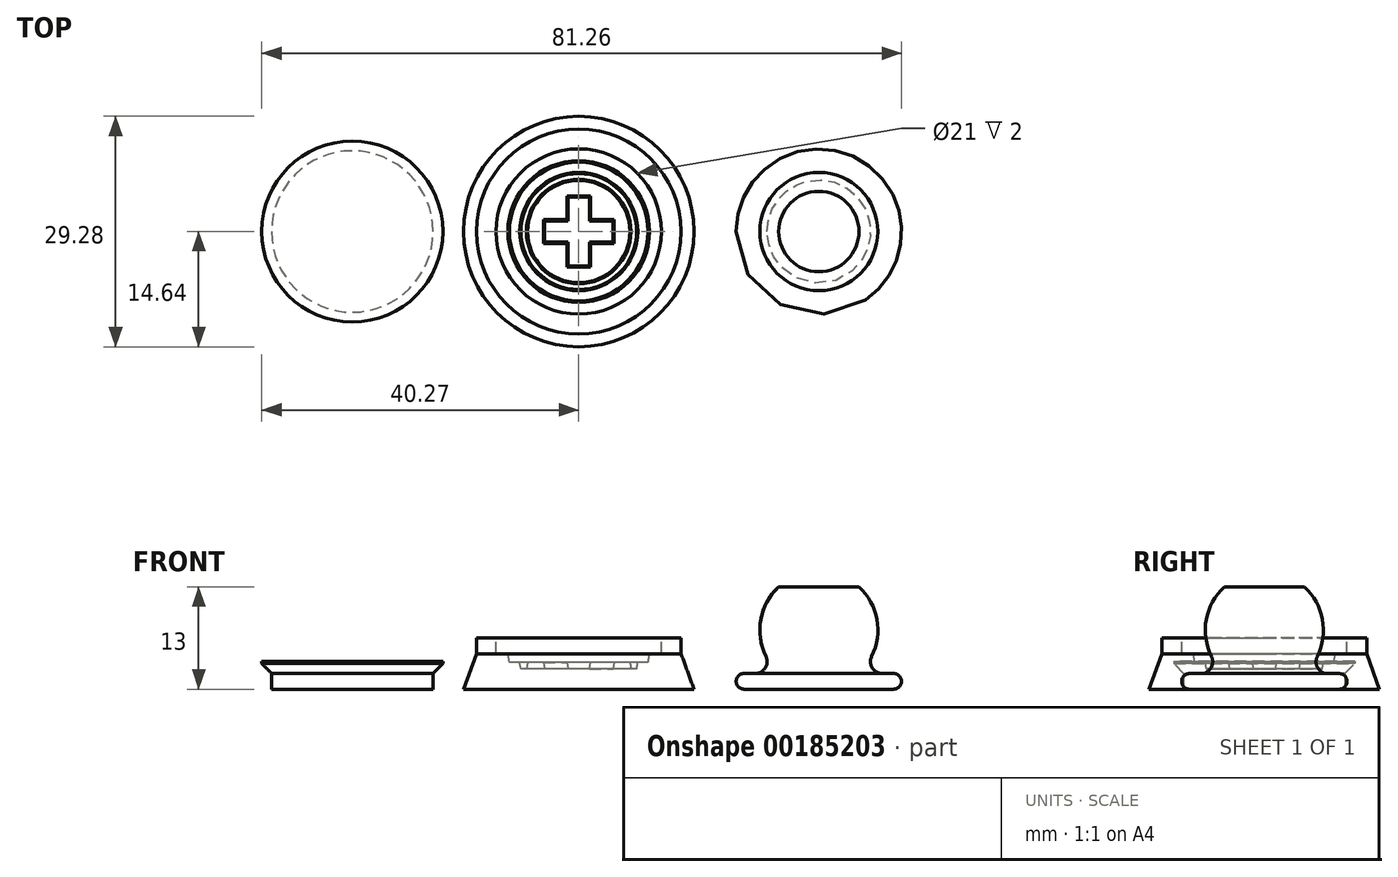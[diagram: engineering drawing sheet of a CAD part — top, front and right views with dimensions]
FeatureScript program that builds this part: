
annotation { "Feature Type Name" : "Feature", "Feature Type Description" : "" }
export const myFeature = defineFeature(function(context is Context, id is Id, definition is map)
    precondition{}
    {
        {
            var Q0;
            Q0=qCreatedBy(makeId("Front.planeOp"),FACE);
            var sketch = newSketch(context, id + "F0", { "sketchPlane" : qUnion([Q0])});
            skLineSegment(sketch, "E0.bottom", {"start": v(-13, 1) * mm, "end": v(0, 1) * mm});
            skLineSegment(sketch, "E0.top", {"start": v(-14.64, -3.5) * mm, "end": v(0, -3.5) * mm});
            skLineSegment(sketch, "E0.right", {"start": v(0, 1) * mm, "end": v(0, -3.5) * mm});
            skLineSegment(sketch, "E1", {"start": v(0, 7.32) * mm, "end": v(0, -8.04) * mm, "construction": true});
            skLineSegment(sketch, "E2", {"start": v(-13, 1) * mm, "end": v(-14.64, -3.5) * mm});
            skSolve(sketch);
        }
        {
            var Q0;
            Q0=makeQuery(id+"F0.imprint","IMPRINT",FACE,{"disambiguationData":[TD([[makeQuery(id+"F0.imprint","IMPRINT",EDGE,{"derivedFrom":sQuery(id+"F0.wireOp",EDGE,"E0.bottom")}),-1.0]])]});
            var Q1;
            Q1=sQuery(id+"F0.wireOp",EDGE,"E1");
            revolve(context, id + "F1", {"entities" : qUnion([Q0]), "axis" : qUnion([Q1]), "revolveType" : RevolveType.FULL});
        }
        {
            var Q0;
            Q0=makeQuery(id+"F1.opRevolve","SWEPT_FACE",FACE,{"disambiguationData":[OSD([sQuery(id+"F0.wireOp",EDGE,"E0.bottom")])]});
            var sketch = newSketch(context, id + "F2", { "sketchPlane" : qUnion([Q0])});
            skCircle(sketch, "E3", {"center": v(0, 0) * mm, "radius": 9 * mm});
            skSolve(sketch);
        }
        {
            var Q0;
            Q0=makeQuery(id+"F2.imprint","IMPRINT",FACE,{"disambiguationData":[TD([[makeQuery(id+"F2.imprint","IMPRINT",EDGE,{"derivedFrom":sQuery(id+"F2.wireOp",EDGE,"E3")}),1.0]])]});
            extrude(context, id + "F3", {"entities" : qUnion([Q0]), "operationType" : NewBodyOperationType.REMOVE, "oppositeDirection" : true, "depth" : 1.1 * mm, "hasDraft" : true, "draftAngle" : 10 * degree, "draftPullDirection" : true});
        }
        {
            var Q0;
            Q0=makeQuery(id+"F3.boolean.opBoolean","COPY",FACE,{"derivedFrom":makeQuery(id+"F3.opExtrude","CAP_FACE",FACE,{"disambiguationData":[OSD([sQuery(id+"F2.wireOp",EDGE,"E3")])],"isStart":false})});
            var sketch = newSketch(context, id + "F4", { "sketchPlane" : qUnion([Q0])});
            skCircle(sketch, "E4", {"center": v(0, 0) * mm, "radius": 7.5 * mm});
            skCircle(sketch, "E5", {"center": v(0, 0) * mm, "radius": 6.5 * mm});
            skLineSegment(sketch, "E6.bottom", {"start": v(-1.5, 4.5) * mm, "end": v(1.5, 4.5) * mm});
            skLineSegment(sketch, "E6.top", {"start": v(-1.5, -4.5) * mm, "end": v(1.5, -4.5) * mm});
            skLineSegment(sketch, "E6.left", {"start": v(-1.5, 4.5) * mm, "end": v(-1.5, 1.5) * mm});
            skLineSegment(sketch, "E6.right", {"start": v(1.5, 4.5) * mm, "end": v(1.5, 1.5) * mm});
            skLineSegment(sketch, "E7.bottom", {"start": v(-4.5, 1.5) * mm, "end": v(-1.5, 1.5) * mm});
            skLineSegment(sketch, "E7.top", {"start": v(-4.5, -1.5) * mm, "end": v(-1.5, -1.5) * mm});
            skLineSegment(sketch, "E7.left", {"start": v(-4.5, 1.5) * mm, "end": v(-4.5, -1.5) * mm});
            skLineSegment(sketch, "E7.right", {"start": v(4.5, 1.5) * mm, "end": v(4.5, -1.5) * mm});
            skLineSegment(sketch, "E8.trimOffspring", {"start": v(1.5, 1.5) * mm, "end": v(4.5, 1.5) * mm});
            skLineSegment(sketch, "E9.trimOffspring", {"start": v(-1.5, -1.5) * mm, "end": v(-1.5, -4.5) * mm});
            skLineSegment(sketch, "E10.trimOffspring", {"start": v(1.5, -1.5) * mm, "end": v(4.5, -1.5) * mm});
            skLineSegment(sketch, "E11.trimOffspring", {"start": v(1.5, -1.5) * mm, "end": v(1.5, -4.5) * mm});
            skSolve(sketch);
        }
        {
            var Q0;
            Q0=makeQuery(id+"F4.imprint","IMPRINT",FACE,{"disambiguationData":[TD([[makeQuery(id+"F4.imprint","IMPRINT",EDGE,{"derivedFrom":sQuery(id+"F4.wireOp",EDGE,"E6.bottom")}),-1.0]])]});
            var Q1;
            Q1=makeQuery(id+"F4.imprint","IMPRINT",FACE,{"disambiguationData":[TD([[makeQuery(id+"F4.imprint","IMPRINT",EDGE,{"derivedFrom":sQuery(id+"F4.wireOp",EDGE,"E4")}),1.0]])]});
            extrude(context, id + "F5", {"entities" : qUnion([Q0, Q1]), "operationType" : NewBodyOperationType.REMOVE, "oppositeDirection" : true, "depth" : .8 * mm, "hasDraft" : true, "draftAngle" : 10 * degree, "draftPullDirection" : true});
        }
        {
            var Q0;
            Q0=qCreatedBy(makeId("Front.planeOp"),FACE);
            var sketch = newSketch(context, id + "F6", { "sketchPlane" : qUnion([Q0])});
            skLineSegment(sketch, "E12", {"start": v(0, 6.95) * mm, "end": v(0, -3.6) * mm, "construction": true});
            skLineSegment(sketch, "E13.bottom", {"start": v(-13, 3) * mm, "end": v(-10.5, 3) * mm});
            skLineSegment(sketch, "E13.top", {"start": v(-13, 1) * mm, "end": v(-10.5, 1) * mm});
            skLineSegment(sketch, "E13.left", {"start": v(-13, 3) * mm, "end": v(-13, 1) * mm});
            skLineSegment(sketch, "E13.right", {"start": v(-10.5, 3) * mm, "end": v(-10.5, 1) * mm});
            skSolve(sketch);
        }
        {
            var Q0;
            Q0=makeQuery(id+"F6.imprint","IMPRINT",FACE,{"disambiguationData":[TD([[makeQuery(id+"F6.imprint","IMPRINT",EDGE,{"derivedFrom":sQuery(id+"F6.wireOp",EDGE,"E13.bottom")}),-1.0]])]});
            var Q1;
            Q1=sQuery(id+"F6.wireOp",EDGE,"E12");
            revolve(context, id + "F7", {"operationType" : NewBodyOperationType.ADD, "entities" : qUnion([Q0]), "axis" : qUnion([Q1]), "revolveType" : RevolveType.FULL});
        }
        {
            var Q0;
            Q0=qCreatedBy(makeId("Front.planeOp"),FACE);
            var sketch = newSketch(context, id + "F8", { "sketchPlane" : qUnion([Q0])});
            skLineSegment(sketch, "E14.top", {"start": v(-39.02, -3.5) * mm, "end": v(-28.77, -3.5) * mm});
            skLineSegment(sketch, "E14.left", {"start": v(-39.02, -1.5) * mm, "end": v(-39.02, -3.5) * mm});
            skLineSegment(sketch, "E14.right", {"start": v(-28.77, -1.3) * mm, "end": v(-28.77, -3.5) * mm});
            skLineSegment(sketch, "E15", {"start": v(-28.77, -6.34) * mm, "end": v(-28.77, 2.62) * mm, "construction": true});
            skLineSegment(sketch, "E16.bottom", {"start": v(-28.77, 0) * mm, "end": v(-40.27, 0) * mm});
            skLineSegment(sketch, "E16.left", {"start": v(-28.77, 0) * mm, "end": v(-28.77, -1.3) * mm});
            skLineSegment(sketch, "E16.right", {"start": v(-40.27, 0) * mm, "end": v(-40.27, -0.25) * mm});
            skLineSegment(sketch, "E17", {"start": v(-40.27, -0.25) * mm, "end": v(-39.02, -1.5) * mm});
            skSolve(sketch);
        }
        {
            var Q0;
            Q0=makeQuery(id+"F8.imprint","IMPRINT",FACE,{"disambiguationData":[TD([[makeQuery(id+"F8.imprint","IMPRINT",EDGE,{"derivedFrom":sQuery(id+"F8.wireOp",EDGE,"E14.top")}),1.0]])]});
            var Q1;
            Q1=sQuery(id+"F8.wireOp",EDGE,"E15");
            revolve(context, id + "F9", {"entities" : qUnion([Q0]), "axis" : qUnion([Q1]), "revolveType" : RevolveType.FULL});
        }
        {
            var Q0;
            Q0=qCreatedBy(makeId("Front.planeOp"),FACE);
            var sketch = newSketch(context, id + "F10", { "sketchPlane" : qUnion([Q0])});
            skLineSegment(sketch, "E18.bottom", {"start": v(21, -1.5) * mm, "end": v(22.43, -1.5) * mm});
            skLineSegment(sketch, "E18.top", {"start": v(21, -3.5) * mm, "end": v(30.5, -3.5) * mm});
            skLineSegment(sketch, "E18.left", {"start": v(20, -2.5) * mm, "end": v(20, -2.5) * mm});
            skLineSegment(sketch, "E19", {"start": v(30.5, -7.79) * mm, "end": v(30.5, -5.66) * mm, "construction": true});
            skArc(sketch, "E20", {"start": v(25.4, 9.5) * mm, "mid": v(23.12, 5.35) * mm, "end": v(23.78, 0.67) * mm});
            skLineSegment(sketch, "E21", {"start": v(30.5, 9.5) * mm, "end": v(30.5, -3.5) * mm});
            skPoint(sketch, "E22.visualSharp", {"position": v(25.4, -1.5) * mm});
            skArc(sketch, "E22.filletArc", {"start": v(22.43, -1.5) * mm, "mid": v(23.7, -0.8) * mm, "end": v(23.78, 0.67) * mm});
            skPoint(sketch, "E23.visualSharp", {"position": v(20, -1.5) * mm});
            skArc(sketch, "E23.filletArc", {"start": v(21, -1.5) * mm, "mid": v(20.29, -1.8) * mm, "end": v(20, -2.5) * mm});
            skPoint(sketch, "E24.visualSharp", {"position": v(20, -3.5) * mm});
            skArc(sketch, "E24.filletArc", {"start": v(20, -2.5) * mm, "mid": v(20.29, -3.2) * mm, "end": v(21, -3.5) * mm});
            skLineSegment(sketch, "E25", {"start": v(25.4, 9.5) * mm, "end": v(30.5, 9.5) * mm});
            skSolve(sketch);
        }
        {
            var Q0;
            Q0=makeQuery(id+"F10.imprint","IMPRINT",FACE,{"disambiguationData":[TD([[makeQuery(id+"F10.imprint","IMPRINT",EDGE,{"derivedFrom":sQuery(id+"F10.wireOp",EDGE,"E18.bottom")}),-1.0]])]});
            var Q1;
            Q1=sQuery(id+"F10.wireOp",EDGE,"E19");
            revolve(context, id + "F11", {"entities" : qUnion([Q0]), "axis" : qUnion([Q1]), "revolveType" : RevolveType.FULL});
        }
    });
